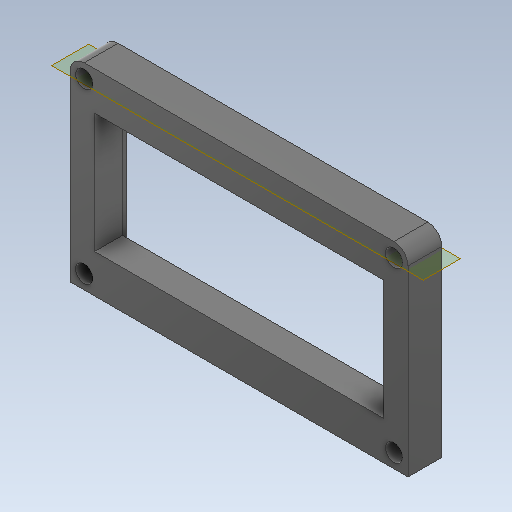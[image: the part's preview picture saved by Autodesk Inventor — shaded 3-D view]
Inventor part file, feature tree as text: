
AUTODESK INVENTOR PART (.ipt)
format: ipt  version: 2020 (Build 240168000, 168)  size: 371,712 bytes
history: native  units: in
note: dims shown in document units (in); Inventor stores cm internally (conversion verified against a paired STEP export)
features: reference x14, sketch x8, other x5, extrude x4, hole x2, plane x2, fillet x1, chamfer x1, helix x1
ambient origin geometry x8: Origin, YZ Plane, XZ Plane, XY Plane, X Axis, Y Axis, Z Axis, Center Point
bodies: Solid1 (feature_tree)
feature tree (38):
  extrude  "Extrusion1"  Depth=4.5in
  hole  "Hole2"  [1 undecoded]
  fillet  "Fillet1"  Radius=0.02in
  sketch  "Sketch3"  dims[d16=0.129in d17=0.75in d18=0.23in d19=0.375in d20=0.5635in d21=1.0in d22=0.8108in d23=0.02in]
  plane  "Work Plane1"
  extrude  "Extrusion4"  Depth=0.015in
  extrude  "Extrusion5"  Depth=0.04in
  extrude  "Extrusion6"  Depth=0.2in TaperAngle=0.0deg
  sketch  "Sketch8"  dims[d33=0.089in d34=0.75in d35=0.23in d36=0.375in d37=0.5635in d38=0.25in d39=0.0in d40=0.0125in d41=0.125in d42=45.0deg]
  hole  "Hole3"  [1 undecoded]
  chamfer  "Chamfer1"  Distance=0.0188in
  plane  "Work Plane2"
  helix  "Coil1"  [1 undecoded]
  sketch  "Sketch Driven Pattern1"  dims[d0=0.45in d1=0.0in d2=4.5in]
  sketch  "Sketch1"  dims[d3=2.621in d11=0.1875in]
  sketch  "Sketch5"  dims[d24=1.0in d25=0.0in d26=0.015in]
  reference  "Reference5"
  reference  "Reference6"
  reference  "Reference7"
  reference  "Reference8"
  reference  "Reference9"
  reference  "Reference10"
  reference  "Reference11"
  reference  "Reference12"
  sketch  "Sketch6"  dims[d27=0.0in d28=0.0in d29=0.04in]
  reference  "Reference13"
  reference  "Reference14"
  sketch  "Sketch7"  dims[d30=0.04in d31=0.2in d32=0.0in]
  reference  "Reference15"
  reference  "Reference16"
  reference  "Reference17"
  reference  "Reference18"
  sketch  "Sketch9"  dims[d43=60.0deg d44=0.0188in d45=0.0063in d46=0.2687in d47=0.025in d48=0.2687in d49=0.3937in d50=0.0in d51=90.0deg d52=90.0deg d53=0.0in d54=0.0in]
  other  "Readout.iam"
  other  "Readout Cover:1"
  other  "Base2:1"
  other  "4x20 LCD:4"
  other  "16 pin header:1"
note: 3 required parameter values undecoded (feature->parameter linkage not recoverable at this tier; creation-order binding heuristic only, values carry confidence <= 0.55)
